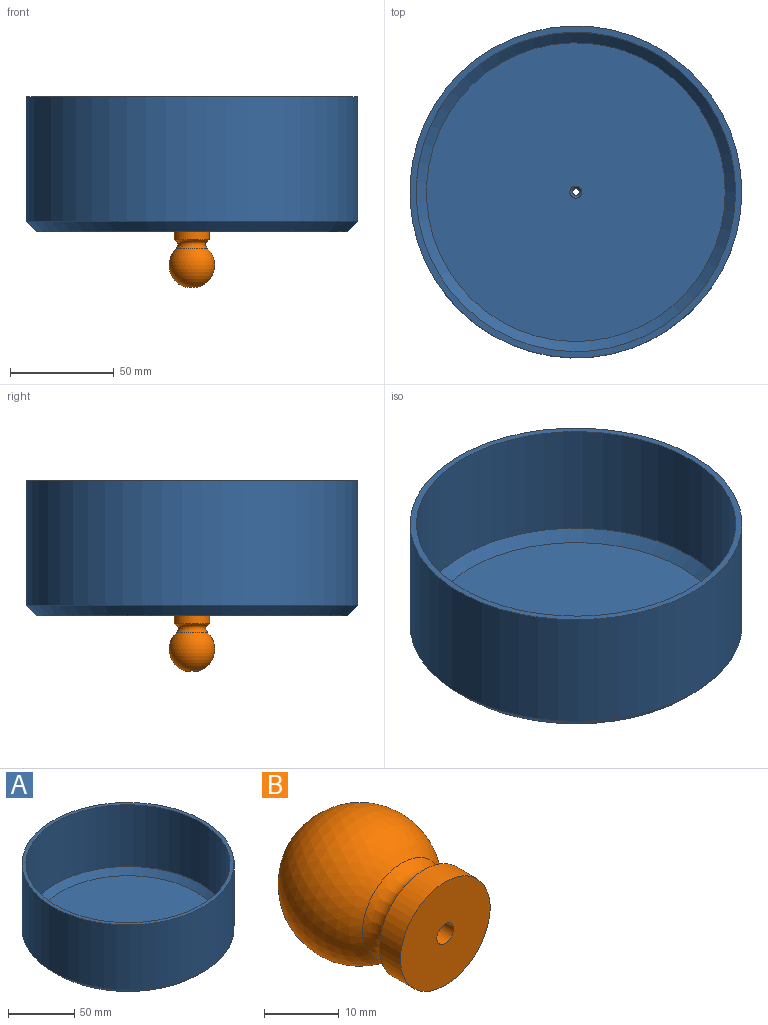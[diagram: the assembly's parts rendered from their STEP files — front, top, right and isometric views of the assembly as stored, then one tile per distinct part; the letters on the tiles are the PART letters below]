
ASSEMBLY  parts=2 mates=1
PART A: 9 faces, bbox 160x160x65 mm
  f0: cylinder r=80mm len=160mm, axis (0,0,-1), area 30159.3mm2, adj f1,f5
  f1: plane 160x160mm, normal (0,0,1), area 1479.7mm2, adj f0,f3
  f2: plane 150x150mm, normal (0,0,-1), area 17663.4mm2, adj f5,f7
  f3: cylinder r=77mm len=154mm, axis (0,0,1), area 27576.9mm2, adj f1,f6
  f4: plane 144x144mm, normal (0,0,1), area 16259.6mm2, adj f6,f8
  f5: cone r=80mm half-angle=45deg, axis (0,0,1), area 3443.2mm2, adj f0,f2
  f6: cone r=72mm half-angle=45deg, axis (0,0,1), area 3309.9mm2, adj f3,f4
  f7: cylinder r=1.6mm len=3.2mm, axis (0,0,1), area 17.1mm2, adj f2,f8
  f8: cone r=1.6mm half-angle=45deg, axis (0,0,1), area 26mm2, adj f4,f7
PART B: 12 faces, bbox 22x26.8x22 mm
  f0: sphere r=11mm, area 1281.8mm2, adj f1,f4,f5,f6,f7,f8,f9
  f1: revolved ~17x17mm, area 240.6mm2, adj f0,f2
  f2: cylinder r=8.5mm len=17mm, axis (0,1,0), area 213.6mm2, adj f1,f3
  f3: plane 17x17mm, normal (0,-1,0), area 218.9mm2, adj f2,f11
  f4: plane 22.76x3mm, normal (-0.87,0,-0.5), area 78.7mm2, adj f0,f5,f9,f10
  f5: plane 22.76x3.46mm, normal (0,0,-1), area 78.7mm2, adj f0,f4,f6,f10
  f6: plane 22.76x3mm, normal (0.87,0,-0.5), area 78.7mm2, adj f0,f5,f7,f10
  f7: plane 22.76x3mm, normal (0.87,0,0.5), area 78.7mm2, adj f0,f6,f8,f10
  f8: plane 22.76x3.46mm, normal (0,0,1), area 78.7mm2, adj f0,f7,f9,f10
  f9: plane 22.76x3mm, normal (-0.87,0,0.5), area 78.7mm2, adj f0,f4,f8,f10
  f10: plane 6.93x6mm, normal (0,1,0), area 23.1mm2, adj f4,f5,f6,f7,f8,f9,f11
  f11: cylinder r=1.6mm len=4mm, axis (0,1,0), area 40.2mm2, adj f3,f10
PLACE A t=(-49.18,11.45,-18.55)mm
PLACE B rot(axis=(-1,0,0),90deg) t=(-49.18,11.45,-18.55)mm
MATE fastened B.f2 <-> A.f0  axis (0,0,1) through (-49.18,11.45,-18.55)mm
